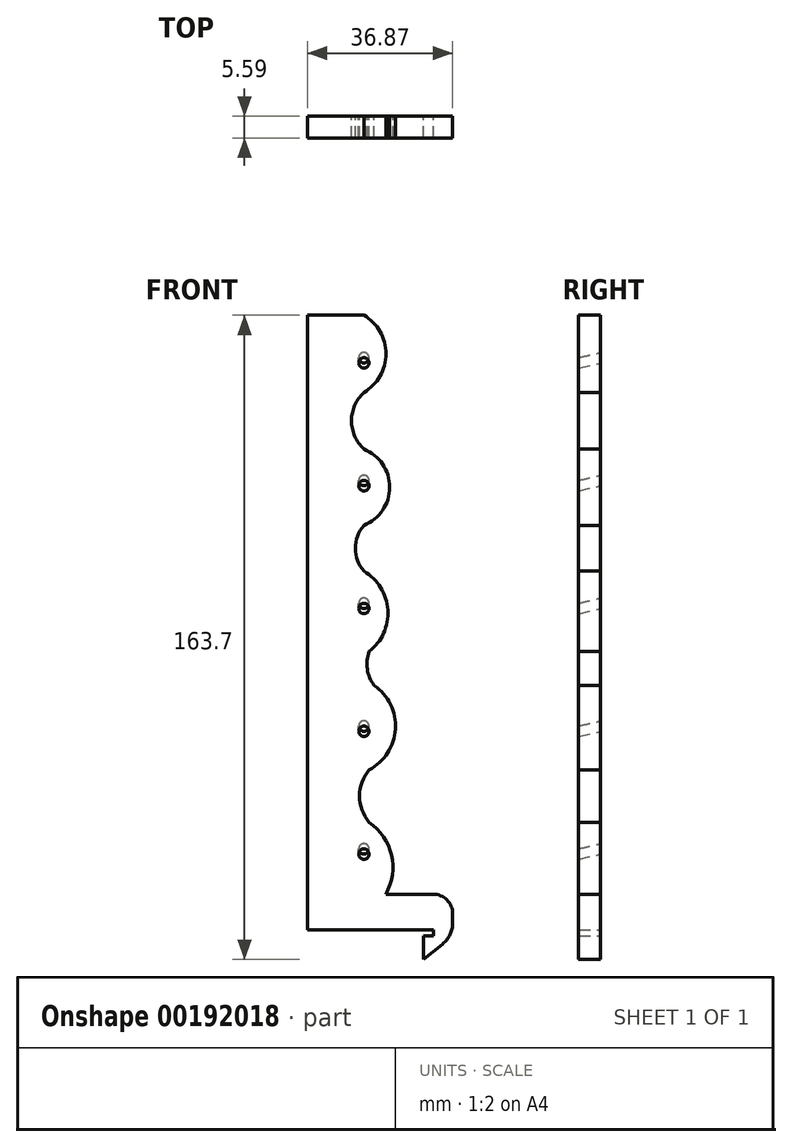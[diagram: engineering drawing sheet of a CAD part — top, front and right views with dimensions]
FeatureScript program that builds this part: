
annotation { "Feature Type Name" : "Feature", "Feature Type Description" : "" }
export const myFeature = defineFeature(function(context is Context, id is Id, definition is map)
    precondition{}
    {
        {
            var Q0;
            Q0=qCreatedBy(makeId("Front.planeOp"),FACE);
            var sketch = newSketch(context, id + "F0", { "sketchPlane" : qUnion([Q0])});
            skLineSegment(sketch, "E0", {"start": v(-18.93, 125.45) * mm, "end": v(-18.93, -30.75) * mm});
            skLineSegment(sketch, "E1", {"start": v(-18.93, 125.45) * mm, "end": v(-4.63, 125.45) * mm});
            skLineSegment(sketch, "E2", {"start": v(10.57, -32.25) * mm, "end": v(13.07, -32.25) * mm});
            skLineSegment(sketch, "E3", {"start": v(-18.93, -30.75) * mm, "end": v(13.07, -30.75) * mm});
            skLineSegment(sketch, "E4", {"start": v(13.07, -32.25) * mm, "end": v(13.07, -30.75) * mm});
            skLineSegment(sketch, "E5", {"start": v(10.57, -32.25) * mm, "end": v(10.57, -38.25) * mm});
            skLineSegment(sketch, "E6", {"start": v(10.57, -38.25) * mm, "end": v(17.94, -32.25) * mm});
            skLineSegment(sketch, "E7", {"start": v(17.94, -32.25) * mm, "end": v(17.94, -21.65) * mm});
            skLineSegment(sketch, "E8", {"start": v(17.94, -21.65) * mm, "end": v(0.94, -21.65) * mm});
            skArc(sketch, "E9", {"start": v(-3.3, 39.97) * mm, "mid": v(-3.75, 35.5) * mm, "end": v(-2, 31.37) * mm});
            skArc(sketch, "E10", {"start": v(-3.3, 9.94) * mm, "mid": v(3.4, 20.28) * mm, "end": v(-2, 31.37) * mm});
            skArc(sketch, "E11", {"start": v(-3.3, 9.94) * mm, "mid": v(-5.71, 3.26) * mm, "end": v(-3.3, -3.41) * mm});
            skArc(sketch, "E12", {"start": v(0.94, -21.65) * mm, "mid": v(2.38, -11.7) * mm, "end": v(-3.3, -3.41) * mm});
            skLineSegment(sketch, "E13", {"start": v(-25.49, -10.15) * mm, "end": v(26.1, -10.15) * mm, "construction": true});
            skLineSegment(sketch, "E14", {"start": v(-28.17, 21.05) * mm, "end": v(27.7, 21.05) * mm, "construction": true});
            skLineSegment(sketch, "E15", {"start": v(-27.9, 52.25) * mm, "end": v(35.76, 52.25) * mm, "construction": true});
            skLineSegment(sketch, "E16", {"start": v(-34.08, 83.45) * mm, "end": v(34.15, 83.45) * mm, "construction": true});
            skLineSegment(sketch, "E17", {"start": v(-33.28, 114.65) * mm, "end": v(32.54, 114.65) * mm, "construction": true});
            skLineSegment(sketch, "E18", {"start": v(-4.63, -52.45) * mm, "end": v(-4.63, 133.2) * mm, "construction": true});
            skArc(sketch, "E19", {"start": v(-3.3, 39.97) * mm, "mid": v(1.47, 50.53) * mm, "end": v(-4.63, 60.4) * mm});
            skArc(sketch, "E20", {"start": v(-4.63, 72.02) * mm, "mid": v(-6.76, 66.2) * mm, "end": v(-4.63, 60.4) * mm});
            skArc(sketch, "E21", {"start": v(-4.63, 72.02) * mm, "mid": v(1.93, 81.73) * mm, "end": v(-4.63, 91.44) * mm});
            skArc(sketch, "E22", {"start": v(-4.63, 105.8) * mm, "mid": v(-7.77, 98.62) * mm, "end": v(-4.63, 91.44) * mm});
            skArc(sketch, "E23", {"start": v(-4.63, 105.8) * mm, "mid": v(0.97, 115.63) * mm, "end": v(-4.63, 125.45) * mm});
            skSolve(sketch);
        }
        {
            var Q0;
            Q0=sQuery(id+"F0.wireOp",EDGE,"E13");
            cPlane(context, id + "F1", {"entities" : qUnion([Q0]), "cplaneType" : CPlaneType.LINE_ANGLE, "offset" : 25 * mm, "angle" : 13.27 * degree, "width" : 150 * mm, "height" : 150 * mm});
        }
        {
            var Q0;
            Q0=sQuery(id+"F0.wireOp",EDGE,"E14");
            cPlane(context, id + "F2", {"entities" : qUnion([Q0]), "cplaneType" : CPlaneType.LINE_ANGLE, "offset" : 25 * mm, "angle" : 13.27 * degree, "width" : 150 * mm, "height" : 150 * mm});
        }
        {
            var Q0;
            Q0=sQuery(id+"F0.wireOp",EDGE,"E15");
            cPlane(context, id + "F3", {"entities" : qUnion([Q0]), "cplaneType" : CPlaneType.LINE_ANGLE, "offset" : 25 * mm, "angle" : 13.27 * degree, "width" : 150 * mm, "height" : 150 * mm});
        }
        {
            var Q0;
            Q0=sQuery(id+"F0.wireOp",EDGE,"E16");
            cPlane(context, id + "F4", {"entities" : qUnion([Q0]), "cplaneType" : CPlaneType.LINE_ANGLE, "offset" : 25 * mm, "angle" : 13.27 * degree, "width" : 150 * mm, "height" : 150 * mm});
        }
        {
            var Q0;
            Q0=sQuery(id+"F0.wireOp",EDGE,"E17");
            cPlane(context, id + "F5", {"entities" : qUnion([Q0]), "cplaneType" : CPlaneType.LINE_ANGLE, "offset" : 25 * mm, "angle" : 13.27 * degree, "width" : 150 * mm, "height" : 150 * mm});
        }
        {
            var Q0;
            Q0=qCreatedBy(id+"F1.planeOp",FACE);
            var sketch = newSketch(context, id + "F6", { "sketchPlane" : qUnion([Q0])});
            skCircle(sketch, "E24", {"center": v(4.63, -9.88) * mm, "radius": 1.3 * mm});
            skSolve(sketch);
        }
        {
            var Q0;
            Q0=qCreatedBy(id+"F2.planeOp",FACE);
            var sketch = newSketch(context, id + "F7", { "sketchPlane" : qUnion([Q0])});
            skCircle(sketch, "E25", {"center": v(4.63, 20.48) * mm, "radius": 1.3 * mm});
            skSolve(sketch);
        }
        {
            var Q0;
            Q0=qCreatedBy(id+"F3.planeOp",FACE);
            var sketch = newSketch(context, id + "F8", { "sketchPlane" : qUnion([Q0])});
            skCircle(sketch, "E26", {"center": v(4.63, 50.85) * mm, "radius": 1.3 * mm});
            skSolve(sketch);
        }
        {
            var Q0;
            Q0=qCreatedBy(id+"F4.planeOp",FACE);
            var sketch = newSketch(context, id + "F9", { "sketchPlane" : qUnion([Q0])});
            skCircle(sketch, "E27", {"center": v(4.63, 81.22) * mm, "radius": 1.3 * mm});
            skSolve(sketch);
        }
        {
            var Q0;
            Q0=qCreatedBy(id+"F5.planeOp",FACE);
            var sketch = newSketch(context, id + "F10", { "sketchPlane" : qUnion([Q0])});
            skCircle(sketch, "E28", {"center": v(4.63, 111.59) * mm, "radius": 1.3 * mm});
            skSolve(sketch);
        }
        {
            var Q0;
            Q0=makeQuery(id+"F0.imprint","IMPRINT",FACE,{"disambiguationData":[TD([[makeQuery(id+"F0.imprint","IMPRINT",EDGE,{"derivedFrom":sQuery(id+"F0.wireOp",EDGE,"E0")}),1.0]])]});
            extrude(context, id + "F11", {"entities" : qUnion([Q0]), "depth" : 5.6 * mm});
        }
        {
            var Q0;
            Q0 = qSketchRegion(id + "F6", true);
            var Q1;
            Q1 = qSketchRegion(id + "F10", true);
            var Q2;
            Q2 = qSketchRegion(id + "F9", true);
            var Q3;
            Q3 = qSketchRegion(id + "F8", true);
            var Q4;
            Q4 = qSketchRegion(id + "F7", true);
            extrude(context, id + "F12", {"entities" : qUnion([Q0, Q1, Q2, Q3, Q4]), "operationType" : NewBodyOperationType.REMOVE, "endBound" : BoundingType.SYMMETRIC, "oppositeDirection" : true, "depth" : 25 * mm});
        }
        {
            var Q0;
            Q0=makeQuery(id+"F11.opExtrude","SWEPT_EDGE",EDGE,{"disambiguationData":[OSD([sQuery(id+"F0.wireOp",EDGE,"E7"),sQuery(id+"F0.wireOp",EDGE,"E8")])]});
            fillet(context, id + "F13", {"entities" : qUnion([Q0]), "radius" : 5 * mm, "tangentPropagation" : true, "allowEdgeOverflow" : false});
        }
        {
            var Q0;
            Q0=makeQuery(id+"F11.opExtrude","SWEPT_EDGE",EDGE,{"disambiguationData":[OSD([sQuery(id+"F0.wireOp",EDGE,"E6"),sQuery(id+"F0.wireOp",EDGE,"E7")])]});
            fillet(context, id + "F14", {"entities" : qUnion([Q0]), "radius" : 7 * mm, "tangentPropagation" : true, "allowEdgeOverflow" : false});
        }
    });
